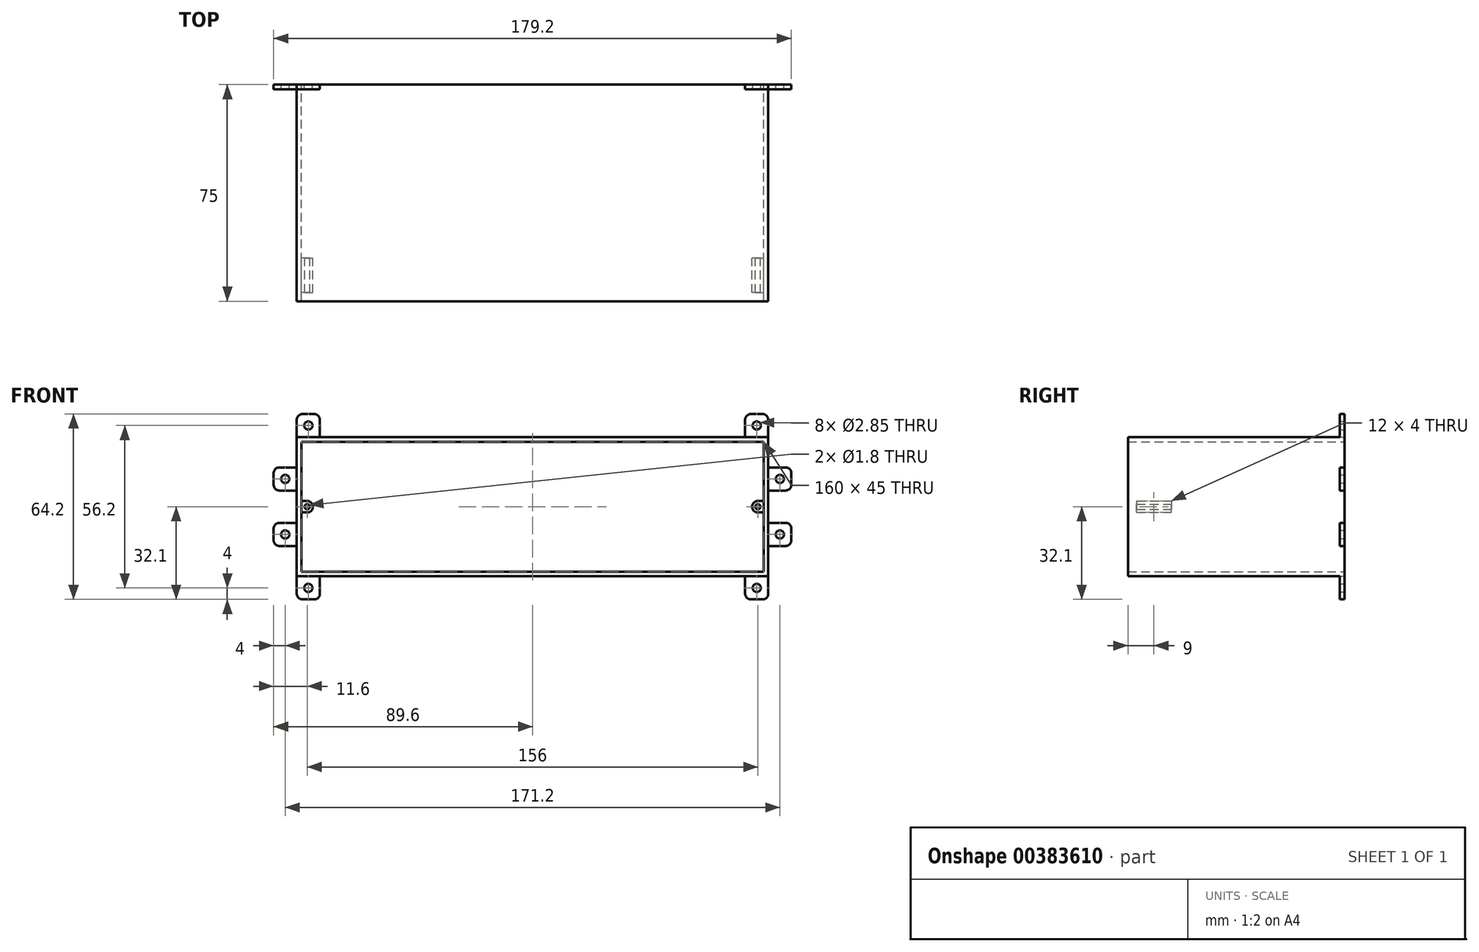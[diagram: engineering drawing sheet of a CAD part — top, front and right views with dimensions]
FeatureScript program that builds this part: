
annotation { "Feature Type Name" : "Feature", "Feature Type Description" : "" }
export const myFeature = defineFeature(function(context is Context, id is Id, definition is map)
    precondition{}
    {
        {
            var Q0;
            Q0=qCreatedBy(makeId("Front.planeOp"),FACE);
            var sketch = newSketch(context, id + "F0", { "sketchPlane" : qUnion([Q0])});
            skLineSegment(sketch, "E0.bottom", {"start": v(80, -22.5) * mm, "end": v(-80, -22.5) * mm});
            skLineSegment(sketch, "E0.top", {"start": v(80, 22.5) * mm, "end": v(-80, 22.5) * mm});
            skLineSegment(sketch, "E0.left", {"start": v(80, -22.5) * mm, "end": v(80, 22.5) * mm});
            skLineSegment(sketch, "E0.right", {"start": v(-80, -22.5) * mm, "end": v(-80, 22.5) * mm});
            skPoint(sketch, "E0.middle", {"position": v(0, 0) * mm});
            skLineSegment(sketch, "E1.0", {"start": v(-81.6, -24.1) * mm, "end": v(-81.6, 24.1) * mm});
            skLineSegment(sketch, "E1.1", {"start": v(81.6, -24.1) * mm, "end": v(-81.6, -24.1) * mm});
            skLineSegment(sketch, "E1.2", {"start": v(81.6, -24.1) * mm, "end": v(81.6, 24.1) * mm});
            skLineSegment(sketch, "E1.3", {"start": v(81.6, 24.1) * mm, "end": v(-81.6, 24.1) * mm});
            skLineSegment(sketch, "E2.bottom", {"start": v(-81.6, 24.1) * mm, "end": v(-73.6, 24.1) * mm});
            skLineSegment(sketch, "E2.top", {"start": v(-81.6, 32.1) * mm, "end": v(-73.6, 32.1) * mm});
            skLineSegment(sketch, "E2.left", {"start": v(-81.6, 24.1) * mm, "end": v(-81.6, 32.1) * mm});
            skLineSegment(sketch, "E2.right", {"start": v(-73.6, 24.1) * mm, "end": v(-73.6, 32.1) * mm});
            skLineSegment(sketch, "E3.bottom", {"start": v(89.6, -13.6) * mm, "end": v(81.6, -13.6) * mm});
            skLineSegment(sketch, "E3.top", {"start": v(89.6, -5.6) * mm, "end": v(81.6, -5.6) * mm});
            skLineSegment(sketch, "E3.left", {"start": v(89.6, -13.6) * mm, "end": v(89.6, -5.6) * mm});
            skPoint(sketch, "E3.middle", {"position": v(81.6, 0) * mm});
            skLineSegment(sketch, "E4.MirrorCS", {"start": v(-81.6, -24.1) * mm, "end": v(-81.6, -32.1) * mm});
            skLineSegment(sketch, "E5.MirrorCS", {"start": v(-81.6, -32.1) * mm, "end": v(-73.6, -32.1) * mm});
            skLineSegment(sketch, "E6.MirrorCS", {"start": v(-73.6, -24.1) * mm, "end": v(-73.6, -32.1) * mm});
            skLineSegment(sketch, "E7.MirrorCS", {"start": v(-81.6, -24.1) * mm, "end": v(-73.6, -24.1) * mm});
            skLineSegment(sketch, "E8.MirrorCS", {"start": v(73.6, 24.1) * mm, "end": v(73.6, 32.1) * mm});
            skLineSegment(sketch, "E9.MirrorCS", {"start": v(81.6, 32.1) * mm, "end": v(73.6, 32.1) * mm});
            skLineSegment(sketch, "E10.MirrorCS", {"start": v(81.6, 24.1) * mm, "end": v(81.6, 32.1) * mm});
            skLineSegment(sketch, "E11.MirrorCS", {"start": v(81.6, 24.1) * mm, "end": v(73.6, 24.1) * mm});
            skLineSegment(sketch, "E12.MirrorCS", {"start": v(81.6, -24.1) * mm, "end": v(73.6, -24.1) * mm});
            skLineSegment(sketch, "E13.MirrorCS", {"start": v(81.6, -24.1) * mm, "end": v(81.6, -32.1) * mm});
            skLineSegment(sketch, "E14.MirrorCS", {"start": v(81.6, -32.1) * mm, "end": v(73.6, -32.1) * mm});
            skLineSegment(sketch, "E15.MirrorCS", {"start": v(73.6, -24.1) * mm, "end": v(73.6, -32.1) * mm});
            skLineSegment(sketch, "E16.MirrorCS", {"start": v(-89.6, -5.6) * mm, "end": v(-81.6, -5.6) * mm});
            skLineSegment(sketch, "E17.MirrorCS", {"start": v(-89.6, -13.6) * mm, "end": v(-89.6, -5.6) * mm});
            skLineSegment(sketch, "E18.MirrorCS", {"start": v(-89.6, -13.6) * mm, "end": v(-81.6, -13.6) * mm});
            skLineSegment(sketch, "E19", {"start": v(-81.6, 32.1) * mm, "end": v(-73.6, 24.1) * mm, "construction": true});
            skLineSegment(sketch, "E20", {"start": v(-73.6, 32.1) * mm, "end": v(-81.6, 24.1) * mm, "construction": true});
            skCircle(sketch, "E21", {"center": v(-77.6, 28.1) * mm, "radius": 1.43 * mm});
            skCircle(sketch, "E22.MirrorC", {"center": v(77.6, 28.1) * mm, "radius": 1.43 * mm});
            skCircle(sketch, "E23.MirrorC", {"center": v(-77.6, -28.1) * mm, "radius": 1.43 * mm});
            skCircle(sketch, "E24.MirrorC", {"center": v(77.6, -28.1) * mm, "radius": 1.43 * mm});
            skLineSegment(sketch, "E25", {"start": v(-89.6, -5.6) * mm, "end": v(-81.6, -13.6) * mm, "construction": true});
            skLineSegment(sketch, "E26", {"start": v(-89.6, -13.6) * mm, "end": v(-81.6, -5.6) * mm, "construction": true});
            skCircle(sketch, "E27", {"center": v(-85.6, -9.6) * mm, "radius": 1.43 * mm});
            skCircle(sketch, "E28.MirrorC", {"center": v(85.6, -9.6) * mm, "radius": 1.43 * mm});
            skLineSegment(sketch, "E29.top", {"start": v(76, -2) * mm, "end": v(80, -2) * mm});
            skLineSegment(sketch, "E29.left", {"start": v(76, 2) * mm, "end": v(76, -2) * mm});
            skPoint(sketch, "E29.middle", {"position": v(80, 0) * mm});
            skLineSegment(sketch, "E30", {"start": v(76, 2) * mm, "end": v(80, 2) * mm});
            skLineSegment(sketch, "E31", {"start": v(80, 2) * mm, "end": v(76, -2) * mm, "construction": true});
            skLineSegment(sketch, "E32", {"start": v(76, 2) * mm, "end": v(80, -2) * mm, "construction": true});
            skCircle(sketch, "E33", {"center": v(78, 0) * mm, "radius": 0.9 * mm});
            skLineSegment(sketch, "E34.MirrorCS", {"start": v(89.6, 13.6) * mm, "end": v(81.6, 13.6) * mm});
            skLineSegment(sketch, "E35.MirrorCS", {"start": v(89.6, 5.6) * mm, "end": v(81.6, 5.6) * mm});
            skLineSegment(sketch, "E36.MirrorCS", {"start": v(89.6, 13.6) * mm, "end": v(89.6, 5.6) * mm});
            skCircle(sketch, "E37.MirrorC", {"center": v(85.6, 9.6) * mm, "radius": 1.43 * mm});
            skLineSegment(sketch, "E38.MirrorCS", {"start": v(-89.6, 5.6) * mm, "end": v(-81.6, 5.6) * mm});
            skLineSegment(sketch, "E39.MirrorCS", {"start": v(-89.6, 13.6) * mm, "end": v(-89.6, 5.6) * mm});
            skLineSegment(sketch, "E40.MirrorCS", {"start": v(-89.6, 13.6) * mm, "end": v(-81.6, 13.6) * mm});
            skCircle(sketch, "E41.MirrorC", {"center": v(-85.6, 9.6) * mm, "radius": 1.43 * mm});
            skSolve(sketch);
        }
        {
            var Q0;
            Q0=makeQuery(id+"F0.imprint","IMPRINT",FACE,{"disambiguationData":[TD([[makeQuery(id+"F0.imprint","IMPRINT",EDGE,{"derivedFrom":sQuery(id+"F0.wireOp",EDGE,"E0.bottom")}),1.0]])]});
            extrude(context, id + "F1", {"entities" : qUnion([Q0]), "depth" : 75 * mm});
        }
        {
            var Q0;
            Q0=qSketchRegion(id+"F0",true);
            extrude(context, id + "F2", {"entities" : qUnion([Q0]), "operationType" : NewBodyOperationType.ADD, "depth" : 1.6 * mm});
        }
        {
            var Q0;
            Q0=makeQuery(id+"F2.opExtrude","SWEPT_EDGE",EDGE,{"disambiguationData":[OSD([sQuery(id+"F0.wireOp",EDGE,"E2.top"),sQuery(id+"F0.wireOp",EDGE,"E2.left")])]});
            var Q1;
            Q1=makeQuery(id+"F2.opExtrude","SWEPT_EDGE",EDGE,{"disambiguationData":[OSD([sQuery(id+"F0.wireOp",EDGE,"E2.top"),sQuery(id+"F0.wireOp",EDGE,"E2.right")])]});
            var Q2;
            Q2=makeQuery(id+"F2.opExtrude","SWEPT_EDGE",EDGE,{"disambiguationData":[OSD([sQuery(id+"F0.wireOp",EDGE,"E8.MirrorCS"),sQuery(id+"F0.wireOp",EDGE,"E9.MirrorCS")])]});
            var Q3;
            Q3=makeQuery(id+"F2.opExtrude","SWEPT_EDGE",EDGE,{"disambiguationData":[OSD([sQuery(id+"F0.wireOp",EDGE,"E9.MirrorCS"),sQuery(id+"F0.wireOp",EDGE,"E10.MirrorCS")])]});
            var Q4;
            Q4=makeQuery(id+"F2.opExtrude","SWEPT_EDGE",EDGE,{"disambiguationData":[OSD([sQuery(id+"F0.wireOp",EDGE,"E3.top"),sQuery(id+"F0.wireOp",EDGE,"E3.left")])]});
            var Q5;
            Q5=makeQuery(id+"F2.opExtrude","SWEPT_EDGE",EDGE,{"disambiguationData":[OSD([sQuery(id+"F0.wireOp",EDGE,"E3.bottom"),sQuery(id+"F0.wireOp",EDGE,"E3.left")])]});
            var Q6;
            Q6=makeQuery(id+"F2.opExtrude","SWEPT_EDGE",EDGE,{"disambiguationData":[OSD([sQuery(id+"F0.wireOp",EDGE,"E13.MirrorCS"),sQuery(id+"F0.wireOp",EDGE,"E14.MirrorCS")])]});
            var Q7;
            Q7=makeQuery(id+"F2.opExtrude","SWEPT_EDGE",EDGE,{"disambiguationData":[OSD([sQuery(id+"F0.wireOp",EDGE,"E14.MirrorCS"),sQuery(id+"F0.wireOp",EDGE,"E15.MirrorCS")])]});
            var Q8;
            Q8=makeQuery(id+"F2.opExtrude","SWEPT_EDGE",EDGE,{"disambiguationData":[OSD([sQuery(id+"F0.wireOp",EDGE,"E17.MirrorCS"),sQuery(id+"F0.wireOp",EDGE,"E18.MirrorCS")])]});
            var Q9;
            Q9=makeQuery(id+"F2.opExtrude","SWEPT_EDGE",EDGE,{"disambiguationData":[OSD([sQuery(id+"F0.wireOp",EDGE,"E16.MirrorCS"),sQuery(id+"F0.wireOp",EDGE,"E17.MirrorCS")])]});
            var Q10;
            Q10=makeQuery(id+"F2.opExtrude","SWEPT_EDGE",EDGE,{"disambiguationData":[OSD([sQuery(id+"F0.wireOp",EDGE,"E4.MirrorCS"),sQuery(id+"F0.wireOp",EDGE,"E5.MirrorCS")])]});
            fillet(context, id + "F3", {"entities" : qUnion([Q0, Q1, Q2, Q3, Q4, Q5, Q6, Q7, Q8, Q9, Q10]), "radius" : 2 * mm, "tangentPropagation" : true, "allowEdgeOverflow" : false});
        }
        {
            var Q0;
            Q0=makeQuery(id+"F1.opExtrude","SWEPT_BODY",BODY,{"disambiguationData":[OSD([sQuery(id+"F0.wireOp",EDGE,"E0.bottom"),sQuery(id+"F0.wireOp",EDGE,"E0.top"),sQuery(id+"F0.wireOp",EDGE,"E0.left"),sQuery(id+"F0.wireOp",EDGE,"E0.right"),sQuery(id+"F0.wireOp",EDGE,"E1.0"),sQuery(id+"F0.wireOp",EDGE,"E1.1"),sQuery(id+"F0.wireOp",EDGE,"E1.2"),sQuery(id+"F0.wireOp",EDGE,"E1.3"),sQuery(id+"F0.wireOp",EDGE,"E2.bottom"),sQuery(id+"F0.wireOp",EDGE,"E7.MirrorCS"),sQuery(id+"F0.wireOp",EDGE,"E11.MirrorCS"),sQuery(id+"F0.wireOp",EDGE,"E12.MirrorCS")])]});
            var Q1;
            Q1=qCreatedBy(makeId("Right.planeOp"),FACE);
            mirror(context, id + "F4", {"operationType" : NewBodyOperationType.ADD, "entities" : qUnion([Q0]), "mirrorPlane" : qUnion([Q1])});
        }
        {
            var Q0;
            Q0=makeQuery(id+"F2.opExtrude","SWEPT_EDGE",EDGE,{"disambiguationData":[OSD([sQuery(id+"F0.wireOp",EDGE,"E5.MirrorCS"),sQuery(id+"F0.wireOp",EDGE,"E6.MirrorCS")])]});
            var Q1;
            Q1=makeQuery(id+"F4.opPattern","COPY",EDGE,{"derivedFrom":makeQuery(id+"F2.opExtrude","SWEPT_EDGE",EDGE,{"disambiguationData":[OSD([sQuery(id+"F0.wireOp",EDGE,"E5.MirrorCS"),sQuery(id+"F0.wireOp",EDGE,"E6.MirrorCS")])]}),"instanceName":"1"});
            fillet(context, id + "F5", {"entities" : qUnion([Q0, Q1]), "radius" : 2 * mm, "tangentPropagation" : true, "allowEdgeOverflow" : false});
        }
        {
            var Q0;
            {var subQ1=sQuery(id+"F0.wireOp",EDGE,"E29.top");Q0=makeQuery(id+"F0.imprint","IMPRINT",FACE,{"disambiguationData":[TD([[makeQuery(id+"F0.imprint","IMPRINT",EDGE,{"derivedFrom":subQ1}),1.0]])]});}
            extrude(context, id + "F6", {"entities" : qUnion([Q0]), "operationType" : NewBodyOperationType.ADD, "depth" : 72 * mm, "hasSecondDirection" : true, "secondDirectionOppositeDirection" : false, "secondDirectionDepth" : 60 * mm});
        }
        {
            var Q0;
            Q0=makeQuery(id+"F6.opExtrude","SWEPT_EDGE",EDGE,{"disambiguationData":[OSD([sQuery(id+"F0.wireOp",EDGE,"E0.left"),sQuery(id+"F0.wireOp",EDGE,"E29.top")])]});
            var Q1;
            Q1=makeQuery(id+"F6.opExtrude","SWEPT_EDGE",EDGE,{"disambiguationData":[OSD([sQuery(id+"F0.wireOp",EDGE,"E29.top"),sQuery(id+"F0.wireOp",EDGE,"E29.left")])]});
            var Q2;
            Q2=makeQuery(id+"F6.opExtrude","SWEPT_EDGE",EDGE,{"disambiguationData":[OSD([sQuery(id+"F0.wireOp",EDGE,"E29.left"),sQuery(id+"F0.wireOp",EDGE,"E30")])]});
            var Q3;
            Q3=makeQuery(id+"F6.opExtrude","SWEPT_EDGE",EDGE,{"disambiguationData":[OSD([sQuery(id+"F0.wireOp",EDGE,"E0.left"),sQuery(id+"F0.wireOp",EDGE,"E30")])]});
            var Q4;
            Q4=makeQuery(id+"F6.opExtrude","CAP_EDGE",EDGE,{"disambiguationData":[OSD([sQuery(id+"F0.wireOp",EDGE,"E0.left")])],"isStart":true});
            fillet(context, id + "F7", {"entities" : qUnion([Q0, Q1, Q2, Q3, Q4]), "radius" : 2 * mm, "tangentPropagation" : true, "allowEdgeOverflow" : false});
        }
        {
            var Q0;
            Q0=makeQuery(id+"F1.opExtrude","SWEPT_BODY",BODY,{"disambiguationData":[OSD([sQuery(id+"F0.wireOp",EDGE,"E0.bottom"),sQuery(id+"F0.wireOp",EDGE,"E0.top"),sQuery(id+"F0.wireOp",EDGE,"E0.left"),sQuery(id+"F0.wireOp",EDGE,"E0.right"),sQuery(id+"F0.wireOp",EDGE,"E1.0"),sQuery(id+"F0.wireOp",EDGE,"E1.1"),sQuery(id+"F0.wireOp",EDGE,"E1.2"),sQuery(id+"F0.wireOp",EDGE,"E1.3"),sQuery(id+"F0.wireOp",EDGE,"E2.bottom"),sQuery(id+"F0.wireOp",EDGE,"E7.MirrorCS"),sQuery(id+"F0.wireOp",EDGE,"E11.MirrorCS"),sQuery(id+"F0.wireOp",EDGE,"E12.MirrorCS")])]});
            var Q1;
            Q1=qCreatedBy(makeId("Right.planeOp"),FACE);
            mirror(context, id + "F8", {"operationType" : NewBodyOperationType.ADD, "entities" : qUnion([Q0]), "mirrorPlane" : qUnion([Q1])});
        }
        {
            var Q0;
            Q0=makeQuery(id+"F2.opExtrude","SWEPT_EDGE",EDGE,{"disambiguationData":[OSD([sQuery(id+"F0.wireOp",EDGE,"E35.MirrorCS"),sQuery(id+"F0.wireOp",EDGE,"E36.MirrorCS")])]});
            var Q1;
            Q1=makeQuery(id+"F2.opExtrude","SWEPT_EDGE",EDGE,{"disambiguationData":[OSD([sQuery(id+"F0.wireOp",EDGE,"E34.MirrorCS"),sQuery(id+"F0.wireOp",EDGE,"E36.MirrorCS")])]});
            var Q2;
            Q2=makeQuery(id+"F2.opExtrude","SWEPT_EDGE",EDGE,{"disambiguationData":[OSD([sQuery(id+"F0.wireOp",EDGE,"E38.MirrorCS"),sQuery(id+"F0.wireOp",EDGE,"E39.MirrorCS")])]});
            var Q3;
            Q3=makeQuery(id+"F2.opExtrude","SWEPT_EDGE",EDGE,{"disambiguationData":[OSD([sQuery(id+"F0.wireOp",EDGE,"E39.MirrorCS"),sQuery(id+"F0.wireOp",EDGE,"E40.MirrorCS")])]});
            fillet(context, id + "F9", {"entities" : qUnion([Q0, Q1, Q2, Q3]), "radius" : 2 * mm, "tangentPropagation" : true, "allowEdgeOverflow" : false});
        }
    });
